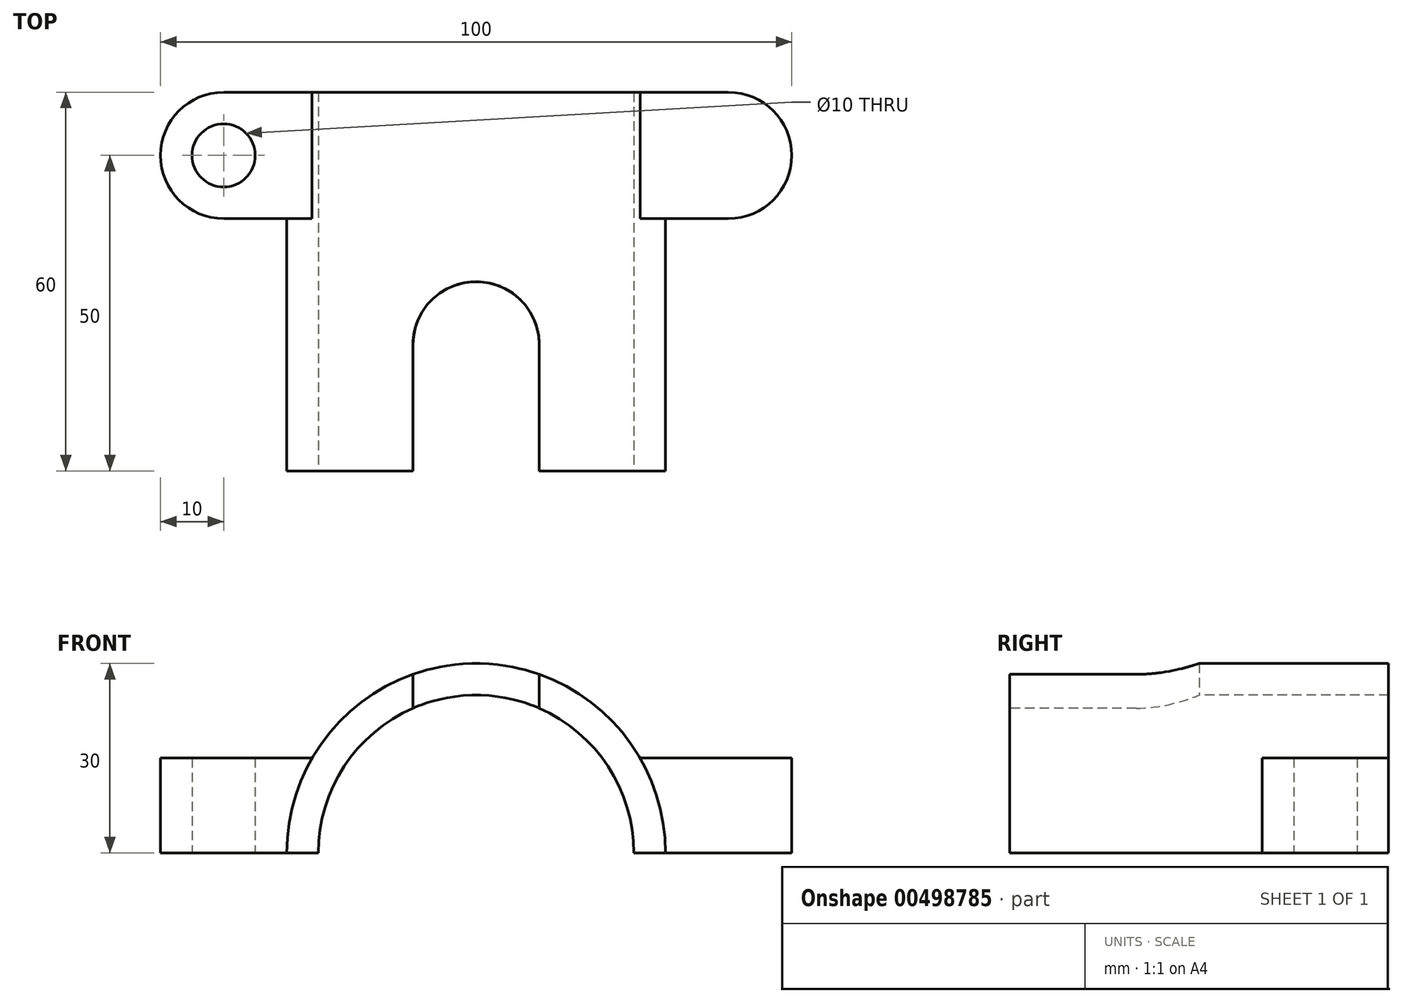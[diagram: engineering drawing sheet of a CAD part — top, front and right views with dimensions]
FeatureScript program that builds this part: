
annotation { "Feature Type Name" : "Feature", "Feature Type Description" : "" }
export const myFeature = defineFeature(function(context is Context, id is Id, definition is map)
    precondition{}
    {
        {
            var Q0;
            Q0=qCreatedBy(makeId("Front.planeOp"),FACE);
            var sketch = newSketch(context, id + "F0", { "sketchPlane" : qUnion([Q0])});
            skArc(sketch, "E0", {"start": v(30, 0) * mm, "mid": v(0, 30) * mm, "end": v(-30, 0) * mm});
            skLineSegment(sketch, "E1", {"start": v(-30, 0) * mm, "end": v(30, 0) * mm});
            skSolve(sketch);
        }
        {
            var Q0;
            Q0=qSketchRegion(id+"F0",true);
            extrude(context, id + "F1", {"entities" : qUnion([Q0]), "oppositeDirection" : true, "depth" : 60 * mm});
        }
        {
            var Q0;
            Q0=qCreatedBy(makeId("Top.planeOp"),FACE);
            var sketch = newSketch(context, id + "F2", { "sketchPlane" : qUnion([Q0])});
            skLineSegment(sketch, "E2", {"start": v(-40, 50) * mm, "end": v(40, 50) * mm, "construction": true});
            skArc(sketch, "E3.0.startCap", {"start": v(-40, 40) * mm, "mid": v(-50, 50) * mm, "end": v(-40, 60) * mm});
            skArc(sketch, "E3.0.endCap", {"start": v(40, 60) * mm, "mid": v(50, 50) * mm, "end": v(40, 40) * mm});
            skLineSegment(sketch, "E3.0.left", {"start": v(-40, 60) * mm, "end": v(40, 60) * mm});
            skLineSegment(sketch, "E3.0.right", {"start": v(-40, 40) * mm, "end": v(40, 40) * mm});
            skPoint(sketch, "E4", {"position": v(0, 50) * mm});
            skSolve(sketch);
        }
        {
            var Q0;
            Q0=qSketchRegion(id+"F2",true);
            extrude(context, id + "F3", {"entities" : qUnion([Q0]), "operationType" : NewBodyOperationType.ADD, "depth" : 15 * mm});
        }
        {
            var Q0;
            Q0=qCreatedBy(makeId("Top.planeOp"),FACE);
            var sketch = newSketch(context, id + "F4", { "sketchPlane" : qUnion([Q0])});
            skCircle(sketch, "E5", {"center": v(-40, 50) * mm, "radius": 5 * mm});
            skSolve(sketch);
        }
        {
            var Q0;
            Q0=qSketchRegion(id+"F4",true);
            extrude(context, id + "F5", {"entities" : qUnion([Q0]), "operationType" : NewBodyOperationType.REMOVE, "endBound" : BoundingType.UP_TO_NEXT, "depth" : 25 * mm});
        }
        {
            var Q0;
            Q0=qCreatedBy(makeId("Top.planeOp"),FACE);
            var sketch = newSketch(context, id + "F6", { "sketchPlane" : qUnion([Q0])});
            skLineSegment(sketch, "E6", {"start": v(-10, 0) * mm, "end": v(-10, 20) * mm});
            skLineSegment(sketch, "E7", {"start": v(-10, 0) * mm, "end": v(0, 0) * mm});
            skLineSegment(sketch, "E8", {"start": v(0, 0) * mm, "end": v(0, 30) * mm});
            skArc(sketch, "E9", {"start": v(-10, 20) * mm, "mid": v(-7.07, 27.07) * mm, "end": v(0, 30) * mm});
            skLineSegment(sketch, "E10", {"start": v(0, 51.89) * mm, "end": v(0, -11.89) * mm, "construction": true});
            skArc(sketch, "E11.MirrorCS", {"start": v(10, 20) * mm, "mid": v(7.07, 27.07) * mm, "end": v(0, 30) * mm});
            skLineSegment(sketch, "E12.MirrorCS", {"start": v(10, 0) * mm, "end": v(10, 20) * mm});
            skLineSegment(sketch, "E13.MirrorCS", {"start": v(10, 0) * mm, "end": v(0, 0) * mm});
            skSolve(sketch);
        }
        {
            var Q0;
            Q0=qSketchRegion(id+"F6",true);
            extrude(context, id + "F7", {"entities" : qUnion([Q0]), "operationType" : NewBodyOperationType.REMOVE, "endBound" : BoundingType.UP_TO_NEXT, "depth" : 25 * mm});
        }
        {
            var Q0;
            {var subQ0=sQuery(id+"F0.wireOp",EDGE,"E0");var subQ1=sQuery(id+"F0.wireOp",EDGE,"E1");Q0=makeQuery(id+"F7.boolean.opBoolean","SPLIT",FACE,{"disambiguationData":[TD([makeQuery(id+"F7.opExtrude","SWEPT_FACE",FACE,{"disambiguationData":[OSD([sQuery(id+"F6.wireOp",EDGE,"E6")])]})])],"derivedFrom":makeQuery(id+"F1.opExtrude","CAP_FACE",FACE,{"disambiguationData":[OSD([subQ0,subQ1])],"isStart":true})});}
            var sketch = newSketch(context, id + "F8", { "sketchPlane" : qUnion([Q0])});
            skCircle(sketch, "E14", {"center": v(0, 0) * mm, "radius": 25 * mm});
            skSolve(sketch);
        }
        {
            var Q0;
            Q0=qSketchRegion(id+"F8",true);
            extrude(context, id + "F9", {"entities" : qUnion([Q0]), "operationType" : NewBodyOperationType.REMOVE, "endBound" : BoundingType.THROUGH_ALL, "oppositeDirection" : true, "depth" : 25 * mm});
        }
    });
